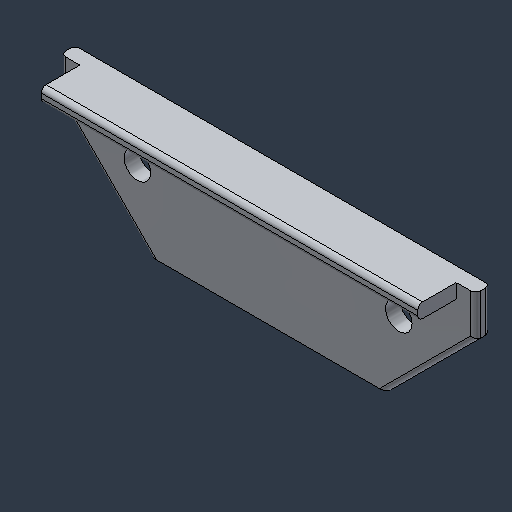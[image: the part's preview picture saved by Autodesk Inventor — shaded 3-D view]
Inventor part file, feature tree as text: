
AUTODESK INVENTOR PART (.ipt)
format: ipt  version: 2024.3 (Build 283343000, 343)  size: 106,496 bytes
history: native  units: mm (DEFAULTED — no unit token found)
features: fillet x1
ambient origin geometry x8: Origin, YZ Plane, XZ Plane, XY Plane, X Axis, Y Axis, Z Axis, Center Point
bodies: Solid1 (feature_tree)
feature tree (1):
  fillet  "Fillet1"  [1 undecoded]
note: 1 required parameter value undecoded (feature->parameter linkage not recoverable at this tier; creation-order binding heuristic only, values carry confidence <= 0.55)
